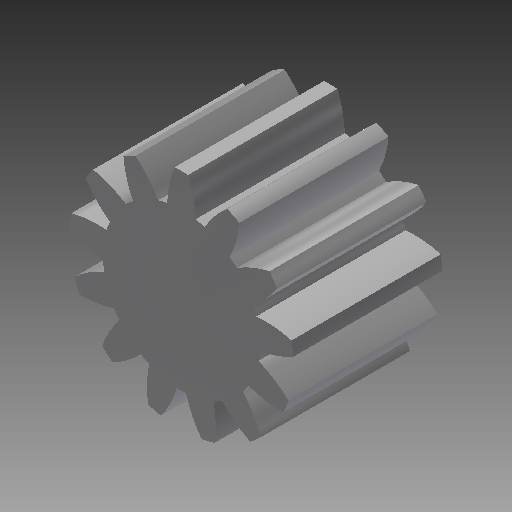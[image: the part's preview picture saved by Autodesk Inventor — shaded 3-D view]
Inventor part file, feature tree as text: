
AUTODESK INVENTOR PART (.ipt)
format: ipt  version: 2017 (Build 210142000, 142)  size: 201,728 bytes
history: native  units: mm (DEFAULTED — no unit token found)
features: plane x3, other x3, sketch x2, extrude x1
ambient origin geometry x8: Origin, YZ Plane, XZ Plane, XY Plane, X Axis, Y Axis, Z Axis, Center Point
bodies: Solid1 (feature_tree)
feature tree (9):
  extrude  "Extrusion1"  Depth=25.4mm TaperAngle=0.0deg
  plane  "Work Plane1"
  plane  "Work Plane2"
  plane  "Work Plane3"
  other  "Spur Gear"
  sketch  "Sketch1"  dims[d0=38.1mm d1=25.4mm d2=0.0mm]
  sketch  "Sketch2"  dims[d3=33.02mm d4=76.2mm d5=0.0mm d6=0.0mm d7=2.41661mm d9=0.0mm d14=0.0mm d15=101.6mm d16=0.0mm d17=0.0mm d18=0.0mm d19=101.6mm]
  other  "Srf1"
  other  "Pitch Diameter"
